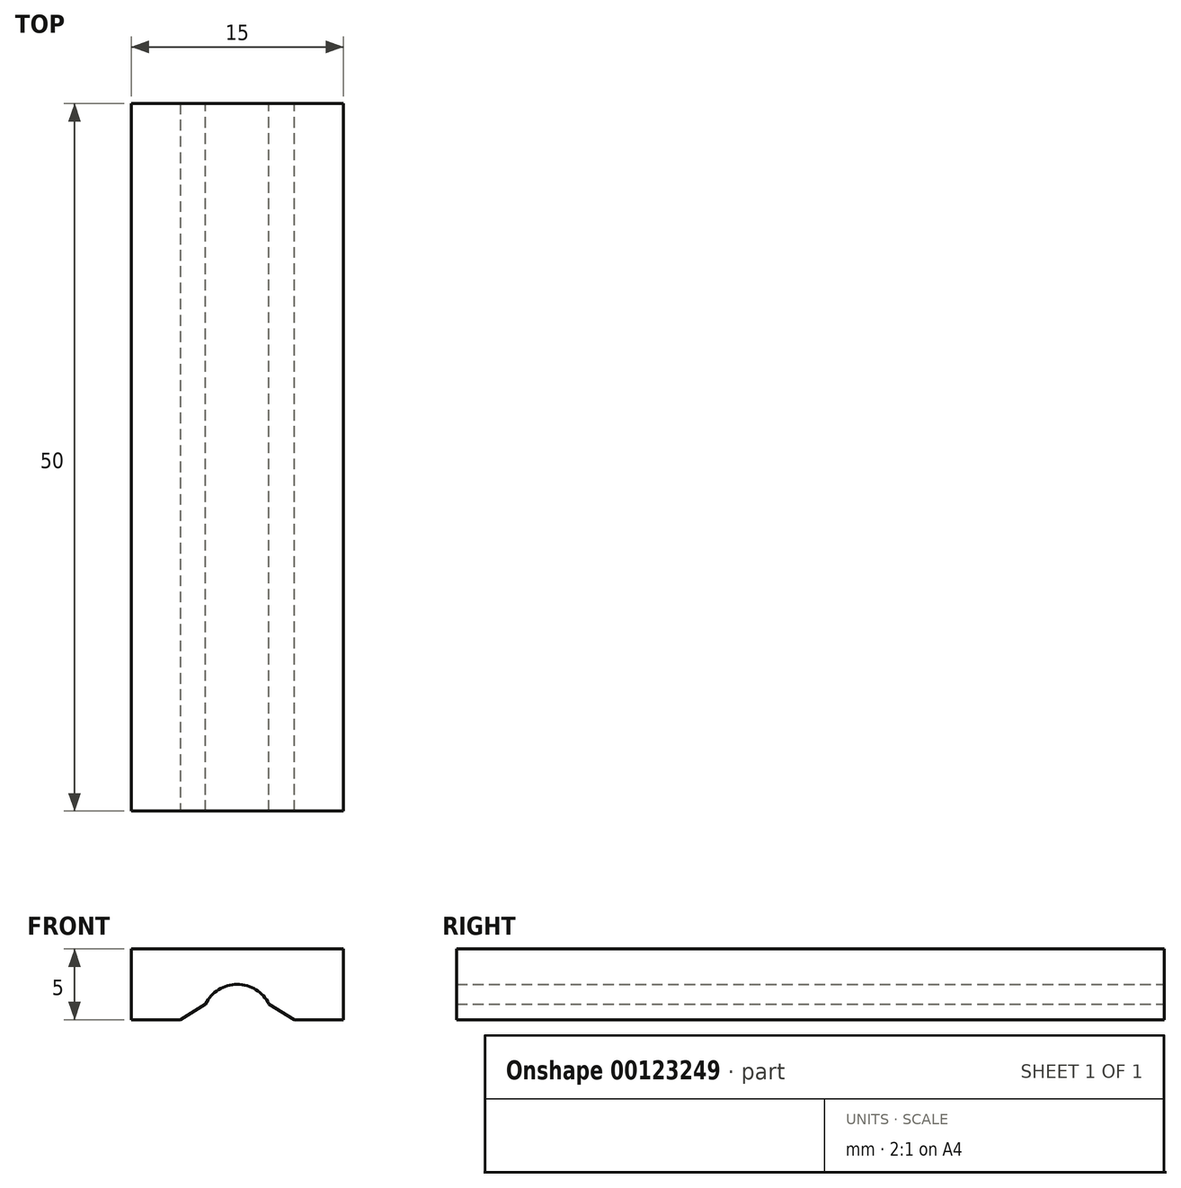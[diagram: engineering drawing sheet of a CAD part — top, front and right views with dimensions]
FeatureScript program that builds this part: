
annotation { "Feature Type Name" : "Feature", "Feature Type Description" : "" }
export const myFeature = defineFeature(function(context is Context, id is Id, definition is map)
    precondition{}
    {
        {
            var Q0;
            Q0=qCreatedBy(makeId("Front.planeOp"),FACE);
            var sketch = newSketch(context, id + "F0", { "sketchPlane" : qUnion([Q0])});
            skLineSegment(sketch, "E0", {"start": v(0, 5) * mm, "end": v(7.5, 5) * mm});
            skLineSegment(sketch, "E1", {"start": v(7.5, 5) * mm, "end": v(7.5, 0) * mm});
            skLineSegment(sketch, "E2", {"start": v(7.5, 0) * mm, "end": v(2.5, 0) * mm});
            skArc(sketch, "E3", {"start": v(2.5, 0) * mm, "mid": v(1.77, 1.77) * mm, "end": v(0, 2.5) * mm});
            skLineSegment(sketch, "E4.MirrorCS", {"start": v(0, 5) * mm, "end": v(-7.5, 5) * mm});
            skLineSegment(sketch, "E5.MirrorCS", {"start": v(-7.5, 5) * mm, "end": v(-7.5, 0) * mm});
            skLineSegment(sketch, "E6.MirrorCS", {"start": v(-7.5, 0) * mm, "end": v(-2.5, 0) * mm});
            skArc(sketch, "E7.MirrorCS", {"start": v(-2.5, 0) * mm, "mid": v(-1.77, 1.77) * mm, "end": v(0, 2.5) * mm});
            skSolve(sketch);
        }
        {
            var Q0;
            Q0=qSketchRegion(id+"F0",true);
            extrude(context, id + "F1", {"entities" : qUnion([Q0]), "depth" : 50 * mm});
        }
        {
            var Q0;
            Q0=makeQuery(id+"F1.opExtrude","SWEPT_EDGE",EDGE,{"disambiguationData":[OSD([sQuery(id+"F0.wireOp",EDGE,"E6.MirrorCS"),sQuery(id+"F0.wireOp",EDGE,"E7.MirrorCS")])]});
            var Q1;
            Q1=makeQuery(id+"F1.opExtrude","SWEPT_EDGE",EDGE,{"disambiguationData":[OSD([sQuery(id+"F0.wireOp",EDGE,"E2"),sQuery(id+"F0.wireOp",EDGE,"E3")])]});
            chamfer(context, id + "F2", {"entities" : qUnion([Q0, Q1]), "width" : 2 * mm, "tangentPropagation" : true});
        }
    });
